# Revit family: ДКУ-20 на ОКК
name_source: partatom
category: Осветительные приборы
units: mm (PartAtom-declared; Revit-internal decimal feet)

## family parameters
Всегда вертикально = Да
Источник света = Да
На основе рабочей плоскости = Нет
Общий = Нет
При загрузке вырезать с полостями = Нет
Размер круглого соединителя = Использовать диаметр
Тип детали = Нормальный
Точка расчета площади = Нет

## types (3) — shared parameters
ADSK_URL страницы изделия = https://www.allfresco.ru
ADSK_Единица измерения = шт.
ADSK_Завод-изготовитель = ALFRESCO
ADSK_Количество фаз = 2
ADSK_Модель = Альф ДКУ-20-AF
ADSK_Напряжение = 220 В
ADSK_Полная мощность = 0 В·А
ADSK_Ток = 0 А
ADSK_Энергоэффективность = 110 лм/Вт
H_дверка = 500 мм
H_конечной точки = 1500 мм
IP Class = IP 67
L_отступ до конечной точки = 1500 мм
L_отступ до центра = 1000 мм
R_дверка = 12 мм
S_дверка = 58 мм
angle = 15.00°
g_дверка = 49 мм
h_дверка = 400 мм
Блок аварийного питания = Нет
Класс защиты = 1
Класс пожароопасности = F (светильники предназначены для установки непосредственно на поверхность из нормально воспламеняемых материалов)
Климатическая зона = УХЛ1
Короб_Диаметр = 20 мм
Корпус светильника = Антрацит
Материал рассеивателя = Светотехнический ПК
Нержавейка = Сталь, хромированная
Область использования = Парки, скверы, общественные пространства, городская инфраструктура
Полная установленная мощность = 0 В·А
Рассеиватель = Белый_светодиод
Светофильтр = 16777215
Смещение цветовой температуры при затухании лампы = <Нет>
Столб_D = 100 мм
Столб_D1 = 60 мм
Столб_поворот_L = 331 мм
Столб_поворот_h = 182 мм
Таблица выбора = Таблица параметров светильников_par2
Температура эксплуатации = -40 +50
Тип ИС = LED-модуль
Тип КСС = тип ШБ (широкая боковая)
Тип ПРА = -
Тип продукции = LED-светильник
Угол наклона = 90.00°
Фланец_H = 8 мм
Цветоывая температура = 2700-5500
zero-valued in all types: ADSK_Количество фаз числовое, ADSK_Коэффициент мощности

## per-type parameters (varying)
| type | ADSK_Артикул | ADSK_Масса | ADSK_Масса_Текст | ADSK_Номинальная мощность | ADSK_Размер_Высота | ADSK_Фактическая мощность | Столб_H | Тип ДКУ | Файл фотометрической сетки | Фланец_L1 | Фланец_L2 | Фланец_отверстие_d |
| ДКУ201 Светодиодный светильник Альф ДКУ-20-AF-30Вт(d48) на опоре ОКК 4м | ДКУ201 | 30 | 30 | 30 Вт | 4000 мм | 28 Вт | 4005 мм | ДКУ_светильник_4м | DKU-20-AF-30W.ies | 230 мм | 190 мм | 18 мм |
| ДКУ202 Светодиодный светильник Альф ДКУ-20-AF-60Вт(d48) на опоре ОКК 6м | ДКУ202 | 48 | 48 | 60 Вт | 6000 мм | 58 Вт | 5994 мм | ДКУ_светильник_6-8м | DKU-20-AF-60W 4000K.ies | 280 мм | 200 мм | 22 мм |
| ДКУ203 Светодиодный светильник Альф ДКУ-20-AF-90Вт(d48) на опоре ОКК 8м | ДКУ203 | 71 | 71 | 90 Вт | 8000 мм | 88 Вт | 7996 мм | ДКУ_светильник_6-8м | DKU-20-AF-90W 4000K.ies | 280 мм | 200 мм | 26 мм |

note: column(s) folded — value = type name in every type: ADSK_Наименование

## geometry (parser evidence)
native form markers: Blend x6
no freeform markers — native parametric forms only
